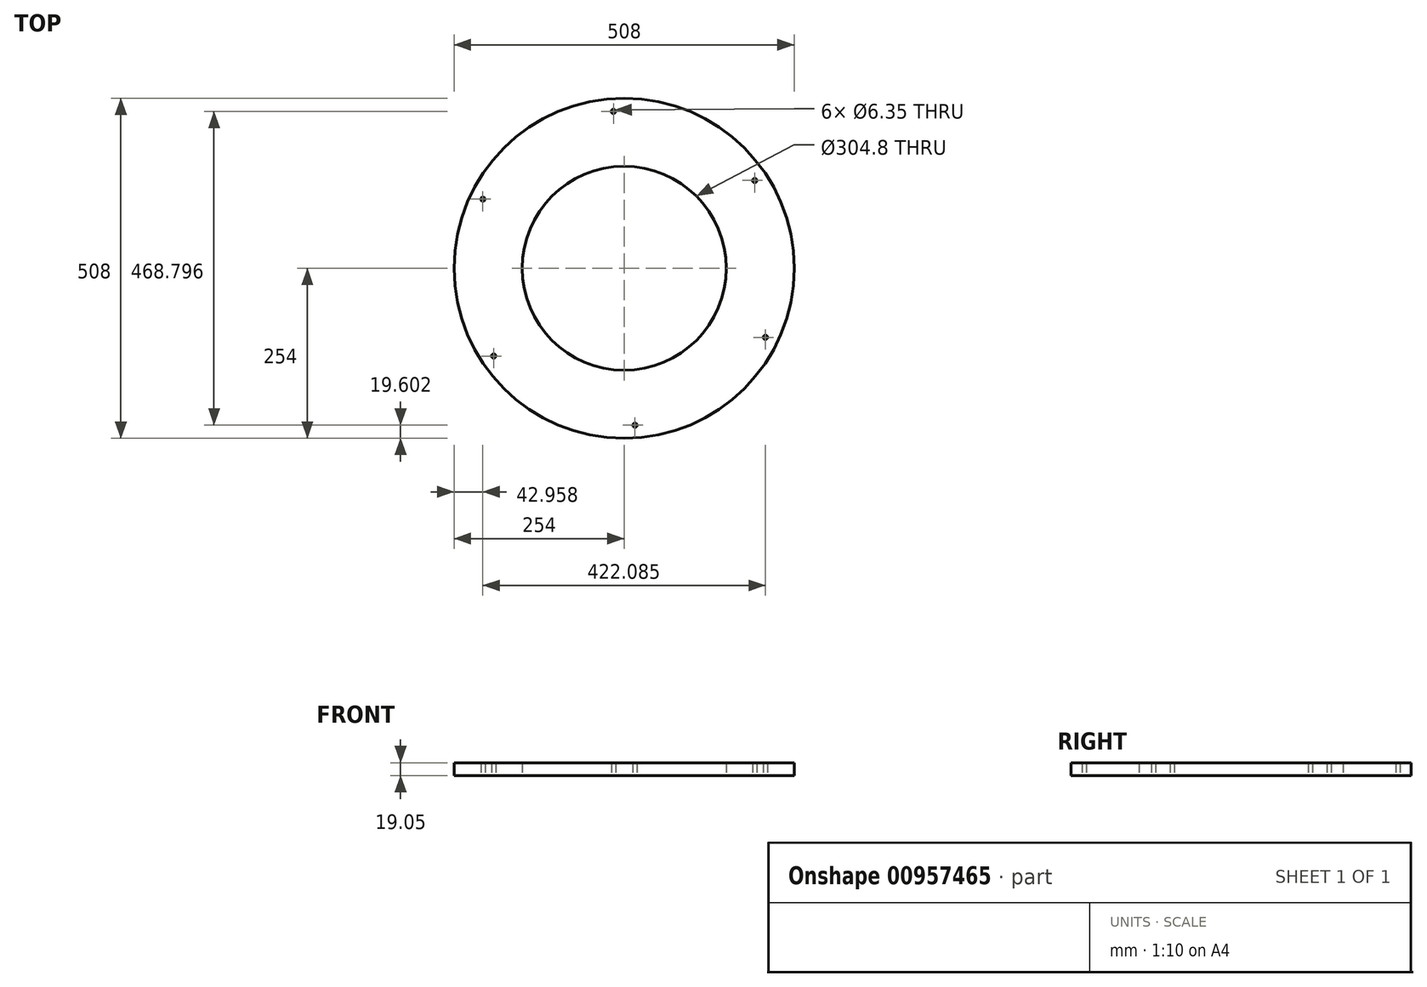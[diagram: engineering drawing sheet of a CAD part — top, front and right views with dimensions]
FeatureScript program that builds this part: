
annotation { "Feature Type Name" : "Feature", "Feature Type Description" : "" }
export const myFeature = defineFeature(function(context is Context, id is Id, definition is map)
    precondition{}
    {
        {
            var Q0;
            Q0=qCreatedBy(makeId("Top.planeOp"),FACE);
            var sketch = newSketch(context, id + "F0", { "sketchPlane" : qUnion([Q0])});
            skCircle(sketch, "E0", {"center": v(0, 0) * mm, "radius": 254 * mm});
            skCircle(sketch, "E1", {"center": v(0, 0) * mm, "radius": 234.95 * mm});
            skCircle(sketch, "E2", {"center": v(-211.04, 103.26) * mm, "radius": 3.18 * mm});
            skCircle(sketch, "E3.1.0", {"center": v(-194.95, -131.14) * mm, "radius": 3.18 * mm});
            skCircle(sketch, "E3.2.0", {"center": v(16.1, -234.4) * mm, "radius": 3.18 * mm});
            skCircle(sketch, "E4.1.3.0", {"center": v(211.04, -103.26) * mm, "radius": 3.18 * mm});
            skCircle(sketch, "E4.1.4.0", {"center": v(194.95, 131.14) * mm, "radius": 3.18 * mm});
            skCircle(sketch, "E4.1.5.0", {"center": v(-16.1, 234.4) * mm, "radius": 3.18 * mm});
            skCircle(sketch, "E5", {"center": v(0, 0) * mm, "radius": 152.4 * mm});
            skSolve(sketch);
        }
        {
            var Q0;
            {var subQ0=sQuery(id+"F0.wireOp",EDGE,"E1");var subQ1=sQuery(id+"F0.wireOp",EDGE,"E2");var subQ5=makeQuery(id+"F0.imprint","INTERSECT",VERTEX,{"disambiguationData":[OD(0.0)],"derivedFrom":[subQ1,subQ0]});Q0=makeQuery(id+"F0.imprint","IMPRINT",FACE,{"disambiguationData":[TD([[makeQuery(id+"F0.imprint","IMPRINT",EDGE,{"disambiguationData":[TD([[subQ5,1.0]])],"derivedFrom":subQ1}),-1.0]])]});}
            var Q1;
            Q1=makeQuery(id+"F0.imprint","IMPRINT",FACE,{"disambiguationData":[TD([[makeQuery(id+"F0.imprint","IMPRINT",EDGE,{"derivedFrom":sQuery(id+"F0.wireOp",EDGE,"E0")}),1.0]])]});
            extrude(context, id + "F1", {"entities" : qUnion([Q0, Q1]), "depth" : 19.05 * mm, "offsetDistance" : 25.4 * mm});
        }
    });
